# Revit family: CVR-S
name_source: partatom
category: Mechanical Equipment
units: mm (PartAtom-declared; Revit-internal decimal feet)

## family parameters
Always vertical = Yes
Cut with Voids When Loaded = No
Part Type = Normal
Room Calculation Point = No
Round Connector Dimension = Use Diameter
Shared = No
Work Plane-Based = No

## types (10) — shared parameters
0 = 0' - 0"
1" = 0' - 1"
1.5 = 0' - 1 1/2"
2" = 0' - 2"
2' = 2' - 0"
3" = 0' - 3"
4" = 0' - 4"
Manufacturer = Loren Cook Company
Model = CVR-S
ONE EIGTH = 0' - 0 1/8"
Type Comments = Centri-Vane All Aluminum Centrifugal Blower Supply Roof Mounted/Belt Drive
URL = www.lorencook.com

## per-type parameters (varying)
- 10_CVR-S: (D+1")/2=0' - 9 3/32"; (SIZE/2)*.66=0' - 3 5/16"; (T_SQ/2)+.125"=0' - 10 1/8"; A=1' - 8 1/8"; A/2=0' - 10 1/16"; B=0' - 4 5/8"; B/2=0' - 2 5/16"; C=1' - 3 1/2"; C/2=0' - 7 3/4"; D=1' - 4 3/16"; D/2=0' - 8 3/32"; E=1' - 3"; E/2=0' - 7 1/2"; F=1' - 6 1/8"; F/2=0' - 9 1/16"; G=0' - 2"; G+(C/2)=0' - 9 3/4"; G+2.5"=1' - 3"; G-.125"=0' - 1 7/8"; RO=1' - 3 1/2"; RO/2=0' - 7 3/4"; SIZE=0' - 10"; SIZE/2=0' - 5"; T_SQ=1' - 8"; T_SQ/2=0' - 10"
- 12_CVR-S: (D+1")/2=0' - 10 9/16"; (SIZE/2)*.66=0' - 3 31/32"; (T_SQ/2)+.125"=0' - 10 1/8"; A=1' - 10 1/8"; A/2=0' - 11 1/16"; B=0' - 5"; B/2=0' - 2 1/2"; C=1' - 5 1/8"; C/2=0' - 8 9/16"; D=1' - 7 1/8"; D/2=0' - 9 9/16"; E=1' - 3"; E/2=0' - 7 1/2"; F=2' - 3 15/16"; F/2=1' - 1 31/32"; G=0' - 2"; G+(C/2)=0' - 10 9/16"; G+2.5"=1' - 4 5/8"; G-.125"=0' - 1 7/8"; RO=1' - 3 1/2"; RO/2=0' - 7 3/4"; SIZE=1' - 0"; SIZE/2=0' - 6"; T_SQ=1' - 8"; T_SQ/2=0' - 10"
- 14_CVR-S: (D+1")/2=1' - 0"; (SIZE/2)*.66=0' - 4 5/8"; (T_SQ/2)+.125"=1' - 0 1/8"; A=2' - 0 1/8"; A/2=1' - 0 1/16"; B=0' - 5"; B/2=0' - 2 1/2"; C=1' - 7 1/8"; C/2=0' - 9 9/16"; D=1' - 10"; D/2=0' - 11"; E=1' - 4"; E/2=0' - 8"; F=2' - 3 15/16"; F/2=1' - 1 31/32"; G=0' - 2"; G+(C/2)=0' - 11 9/16"; G+2.5"=1' - 6 5/8"; G-.125"=0' - 1 7/8"; RO=1' - 7 1/2"; RO/2=0' - 9 3/4"; SIZE=1' - 2"; SIZE/2=0' - 7"; T_SQ=2' - 0"; T_SQ/2=1' - 0"
- 16_CVR-S: (D+1")/2=1' - 1 7/16"; (SIZE/2)*.66=0' - 5 9/32"; (T_SQ/2)+.125"=1' - 0 1/8"; A=2' - 2 9/16"; A/2=1' - 1 9/32"; B=0' - 5"; B/2=0' - 2 1/2"; C=1' - 9 9/16"; C/2=0' - 10 25/32"; D=2' - 0 7/8"; D/2=1' - 0 7/16"; E=1' - 5"; E/2=0' - 8 1/2"; F=2' - 3 15/16"; F/2=1' - 1 31/32"; G=0' - 2"; G+(C/2)=1' - 0 25/32"; G+2.5"=1' - 9 1/16"; G-.125"=0' - 1 7/8"; RO=1' - 7 1/2"; RO/2=0' - 9 3/4"; SIZE=1' - 4"; SIZE/2=0' - 8"; T_SQ=2' - 0"; T_SQ/2=1' - 0"
- 18_CVR-S: (D+1")/2=1' - 2 7/8"; (SIZE/2)*.66=0' - 5 15/16"; (T_SQ/2)+.125"=1' - 2 1/8"; A=2' - 5 1/2"; A/2=1' - 2 3/4"; B=0' - 5"; B/2=0' - 2 1/2"; C=2' - 0 1/2"; C/2=1' - 0 1/4"; D=2' - 3 3/4"; D/2=1' - 1 7/8"; E=1' - 7"; E/2=0' - 9 1/2"; F=2' - 3 15/16"; F/2=1' - 1 31/32"; G=0' - 2"; G+(C/2)=1' - 2 1/4"; G+2.5"=2' - 0"; G-.125"=0' - 1 7/8"; RO=1' - 11 1/2"; RO/2=0' - 11 3/4"; SIZE=1' - 6"; SIZE/2=0' - 9"; T_SQ=2' - 4"; T_SQ/2=1' - 2"
- 20_CVR-S: (D+1")/2=1' - 4 1/4"; (SIZE/2)*.66=0' - 6 19/32"; (T_SQ/2)+.125"=1' - 2 1/8"; A=2' - 9 1/4"; A/2=1' - 4 5/8"; B=0' - 6 3/4"; B/2=0' - 3 3/8"; C=2' - 2 1/2"; C/2=1' - 1 1/4"; D=2' - 6 1/2"; D/2=1' - 3 1/4"; E=1' - 7"; E/2=0' - 9 1/2"; F=3' - 0"; F/2=1' - 6"; G=0' - 2"; G+(C/2)=1' - 3 1/4"; G+2.5"=2' - 2"; G-.125"=0' - 1 7/8"; RO=1' - 11 1/2"; RO/2=0' - 11 3/4"; SIZE=1' - 8"; SIZE/2=0' - 10"; T_SQ=2' - 4"; T_SQ/2=1' - 2"
- 24_CVR-S: (D+1")/2=1' - 7 1/4"; (SIZE/2)*.66=0' - 7 29/32"; (T_SQ/2)+.125"=1' - 4 1/8"; A=3' - 2 1/8"; A/2=1' - 7 1/16"; B=0' - 6 3/4"; B/2=0' - 3 3/8"; C=2' - 7 3/8"; C/2=1' - 3 11/16"; D=3' - 0 1/2"; D/2=1' - 6 1/4"; E=1' - 9"; E/2=0' - 10 1/2"; F=3' - 0"; F/2=1' - 6"; G=0' - 3"; G+(C/2)=1' - 6 11/16"; G+2.5"=2' - 7 7/8"; G-.125"=0' - 2 7/8"; RO=2' - 3 1/2"; RO/2=1' - 1 3/4"; SIZE=2' - 0"; SIZE/2=1' - 0"; T_SQ=2' - 8"; T_SQ/2=1' - 4"
- 28_CVR-S: (D+1")/2=1' - 10"; (SIZE/2)*.66=0' - 9 1/4"; (T_SQ/2)+.125"=1' - 6 1/8"; A=3' - 8"; A/2=1' - 10"; B=0' - 8"; B/2=0' - 4"; C=3' - 0"; C/2=1' - 6"; D=3' - 6"; D/2=1' - 9"; E=2' - 5"; E/2=1' - 2 1/2"; F=3' - 6 1/8"; F/2=1' - 9 1/16"; G=0' - 3"; G+(C/2)=1' - 9"; G+2.5"=3' - 0 1/2"; G-.125"=0' - 2 7/8"; RO=2' - 7 1/2"; RO/2=1' - 3 3/4"; SIZE=2' - 4"; SIZE/2=1' - 2"; T_SQ=3' - 0"; T_SQ/2=1' - 6"
- 32_CVR-S: (D+1")/2=2' - 1"; (SIZE/2)*.66=0' - 10 9/16"; (T_SQ/2)+.125"=1' - 9 1/8"; A=4' - 9 7/8"; A/2=2' - 4 15/16"; B=1' - 5"; B/2=0' - 8 1/2"; C=3' - 4 7/8"; C/2=1' - 8 7/16"; D=4' - 0"; D/2=2' - 0"; E=2' - 6"; E/2=1' - 3"; F=4' - 4"; F/2=2' - 2"; G=0' - 3"; G+(C/2)=1' - 11 7/16"; G+2.5"=3' - 5 3/8"; G-.125"=0' - 2 7/8"; RO=3' - 1 1/2"; RO/2=1' - 6 3/4"; SIZE=2' - 8"; SIZE/2=1' - 4"; T_SQ=3' - 6"; T_SQ/2=1' - 9"
- 36_CVR-S: (D+1")/2=2' - 3 11/16"; (SIZE/2)*.66=0' - 10 9/16"; (T_SQ/2)+.125"=2' - 0 1/8"; A=5' - 1 1/2"; A/2=2' - 6 3/4"; B=1' - 5 1/2"; B/2=0' - 8 3/4"; C=3' - 8"; C/2=1' - 10"; D=4' - 5 3/8"; D/2=2' - 2 11/16"; E=2' - 8"; E/2=1' - 4"; F=5' - 2"; F/2=2' - 7"; G=0' - 3"; G+(C/2)=2' - 1"; G+2.5"=3' - 8 1/2"; G-.125"=0' - 2 7/8"; RO=3' - 7 1/2"; RO/2=1' - 9 3/4"; SIZE=2' - 8"; SIZE/2=1' - 4"; T_SQ=4' - 0"; T_SQ/2=2' - 0"

## geometry (parser evidence)
native form markers: Sweep x2
no freeform markers — native parametric forms only
